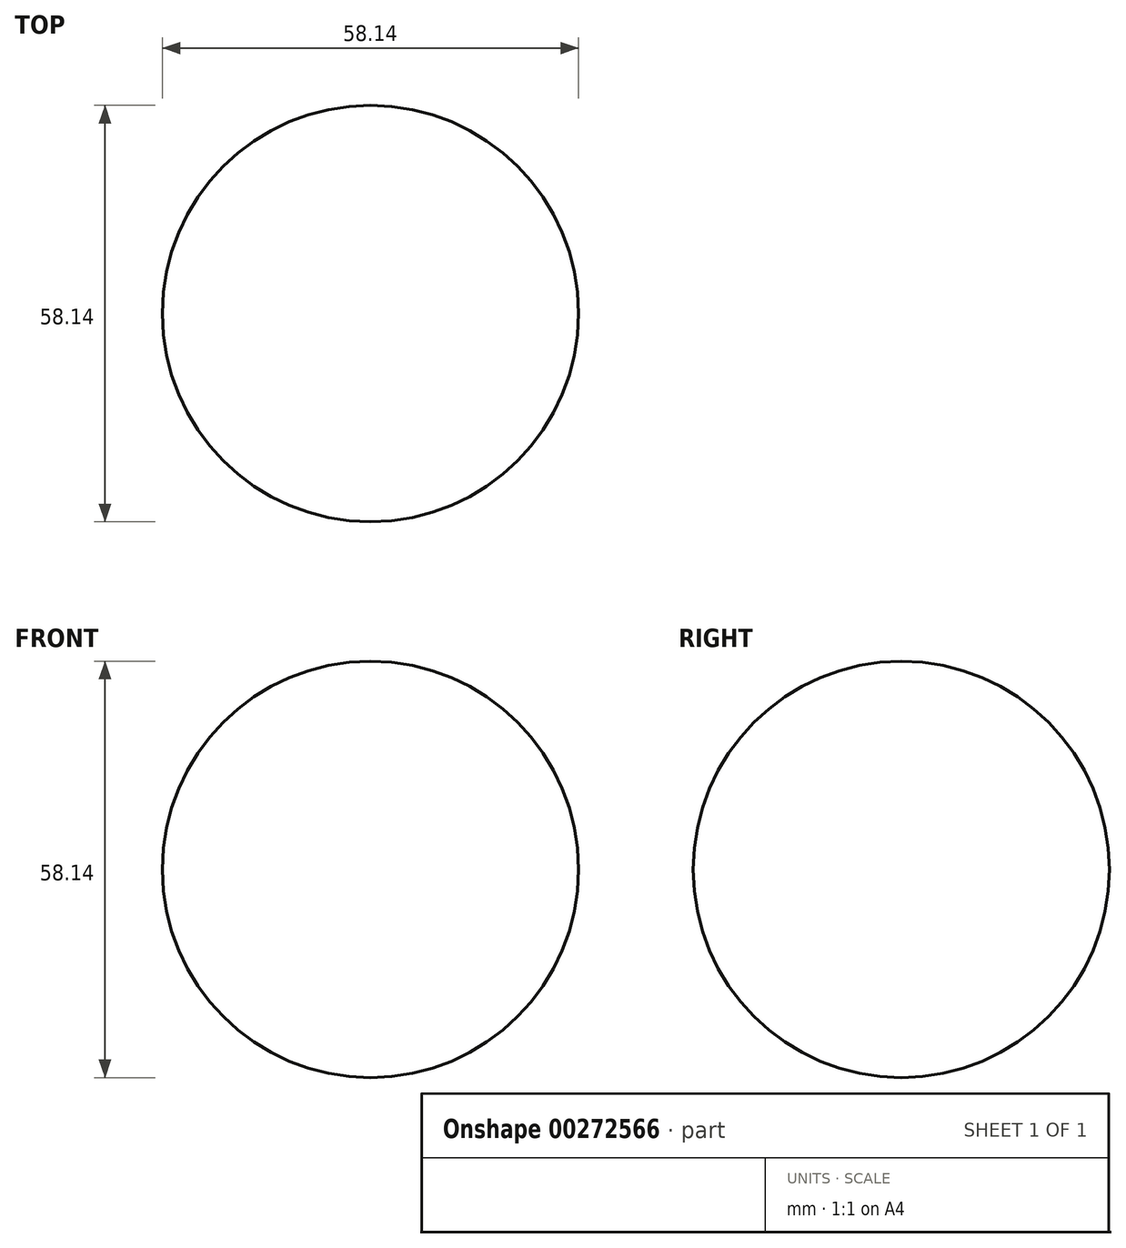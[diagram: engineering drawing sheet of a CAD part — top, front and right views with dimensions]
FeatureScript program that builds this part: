
annotation { "Feature Type Name" : "Feature", "Feature Type Description" : "" }
export const myFeature = defineFeature(function(context is Context, id is Id, definition is map)
    precondition{}
    {
        {
            var Q0;
            Q0=qCreatedBy(makeId("Front.planeOp"),FACE);
            var sketch = newSketch(context, id + "F0", { "sketchPlane" : qUnion([Q0])});
            skArc(sketch, "E0", {"start": v(0, -29.07) * mm, "mid": v(29.07, 0) * mm, "end": v(0, 29.07) * mm});
            skLineSegment(sketch, "E1", {"start": v(0, 29.07) * mm, "end": v(0, -29.07) * mm});
            skSolve(sketch);
        }
        {
            var Q0;
            Q0=makeQuery(id+"F0.imprint","IMPRINT",FACE,{"disambiguationData":[TD([[makeQuery(id+"F0.imprint","IMPRINT",EDGE,{"derivedFrom":sQuery(id+"F0.wireOp",EDGE,"E0")}),1.0]])]});
            var Q1;
            Q1=sQuery(id+"F0.wireOp",EDGE,"E1");
            revolve(context, id + "F1", {"entities" : qUnion([Q0]), "axis" : qUnion([Q1]), "revolveType" : RevolveType.FULL});
        }
    });
